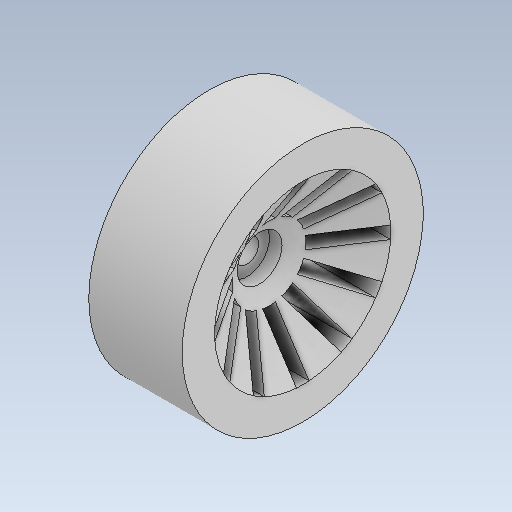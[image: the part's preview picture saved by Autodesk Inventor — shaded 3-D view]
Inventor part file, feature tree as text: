
AUTODESK INVENTOR PART (.ipt)
format: ipt  version: 2021 (Build 250183000, 183)  size: 232,960 bytes
history: native  units: mm
features: other x2, revolve x1, extrude x1, pattern_circular x1, sketch x1
ambient origin geometry x8: Origin, YZ Plane, XZ Plane, XY Plane, X Axis, Y Axis, Z Axis, Center Point
bodies: Volumenkörper1 (feature_tree)
feature tree (6):
  other  "00_Mastersketch.ipt"
  revolve  "Umdrehung1"
  extrude  "Extrusion1"  Depth=3.5mm
  pattern_circular  "Runde Anordnung1"  Angle=90.0deg  [1 undecoded]
  other  "05_wheelSketch"
  sketch  "Skizze2"  dims[d0=10.0mm d1=9.0mm d2=90.0deg d3=3.5mm d4=0.0mm d5=0.0mm d6=120.0mm d7=360.0deg d10=3.0mm d14=4.0mm]
note: 1 required parameter value undecoded (feature->parameter linkage not recoverable at this tier; creation-order binding heuristic only, values carry confidence <= 0.55)
